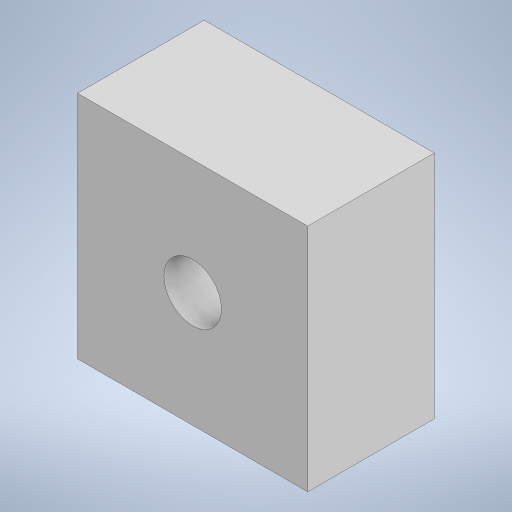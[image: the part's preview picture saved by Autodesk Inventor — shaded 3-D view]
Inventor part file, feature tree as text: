
AUTODESK INVENTOR PART (.ipt)
format: ipt  version: 2023 (Build 270158000, 158)  size: 209,920 bytes
history: native  units: in
note: dims shown in document units (in); Inventor stores cm internally (conversion verified against a paired STEP export)
features: extrude x2, sketch x2
ambient origin geometry x8: Origin, YZ Plane, XZ Plane, XY Plane, X Axis, Y Axis, Z Axis, Center Point
bodies: Body1 (feature_tree)
feature tree (4):
  extrude  "Extrusion2"  Depth=0.7874in
  extrude  "Extrusion3"  Depth=0.3937in
  sketch  "Sketch1"  dims[d0=0.7874in d1=0.7874in]
  sketch  "Sketch3"  dims[d5=0.3937in d6=0.3937in d7=0.1969in d8=0.1969in d9=0.0in d10=0.3543in d11=0.2362in d12=0.0in]
